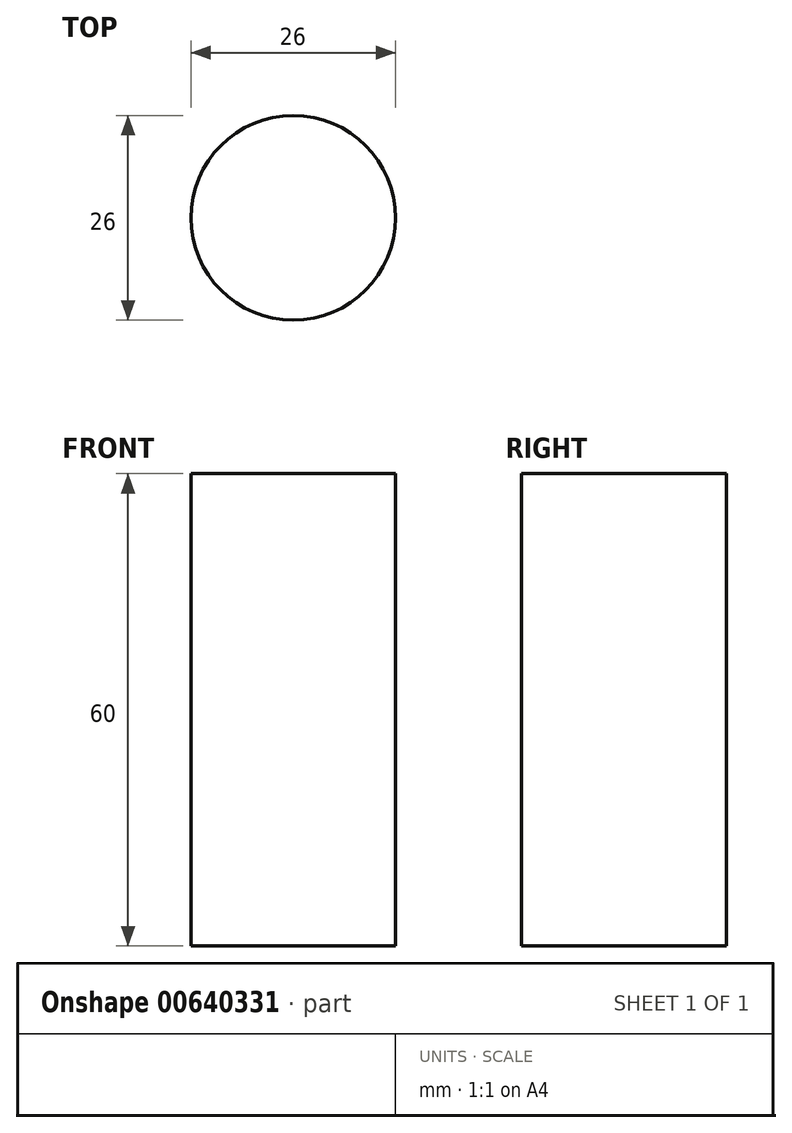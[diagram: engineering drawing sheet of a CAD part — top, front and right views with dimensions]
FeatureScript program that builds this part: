
annotation { "Feature Type Name" : "Feature", "Feature Type Description" : "" }
export const myFeature = defineFeature(function(context is Context, id is Id, definition is map)
    precondition{}
    {
        {
            var Q0;
            Q0=qCreatedBy(makeId("Top.planeOp"),FACE);
            var sketch = newSketch(context, id + "F0", { "sketchPlane" : qUnion([Q0])});
            skCircle(sketch, "E0", {"center": v(0, 0) * mm, "radius": 13 * mm});
            skSolve(sketch);
        }
        {
            var Q0;
            Q0=makeQuery(id+"F0.imprint","IMPRINT",FACE,{"disambiguationData":[TD([[makeQuery(id+"F0.imprint","IMPRINT",EDGE,{"derivedFrom":sQuery(id+"F0.wireOp",EDGE,"E0")}),1.0]])]});
            extrude(context, id + "F1", {"entities" : qUnion([Q0]), "depth" : 60 * mm, "offsetDistance" : 25 * mm});
        }
    });
